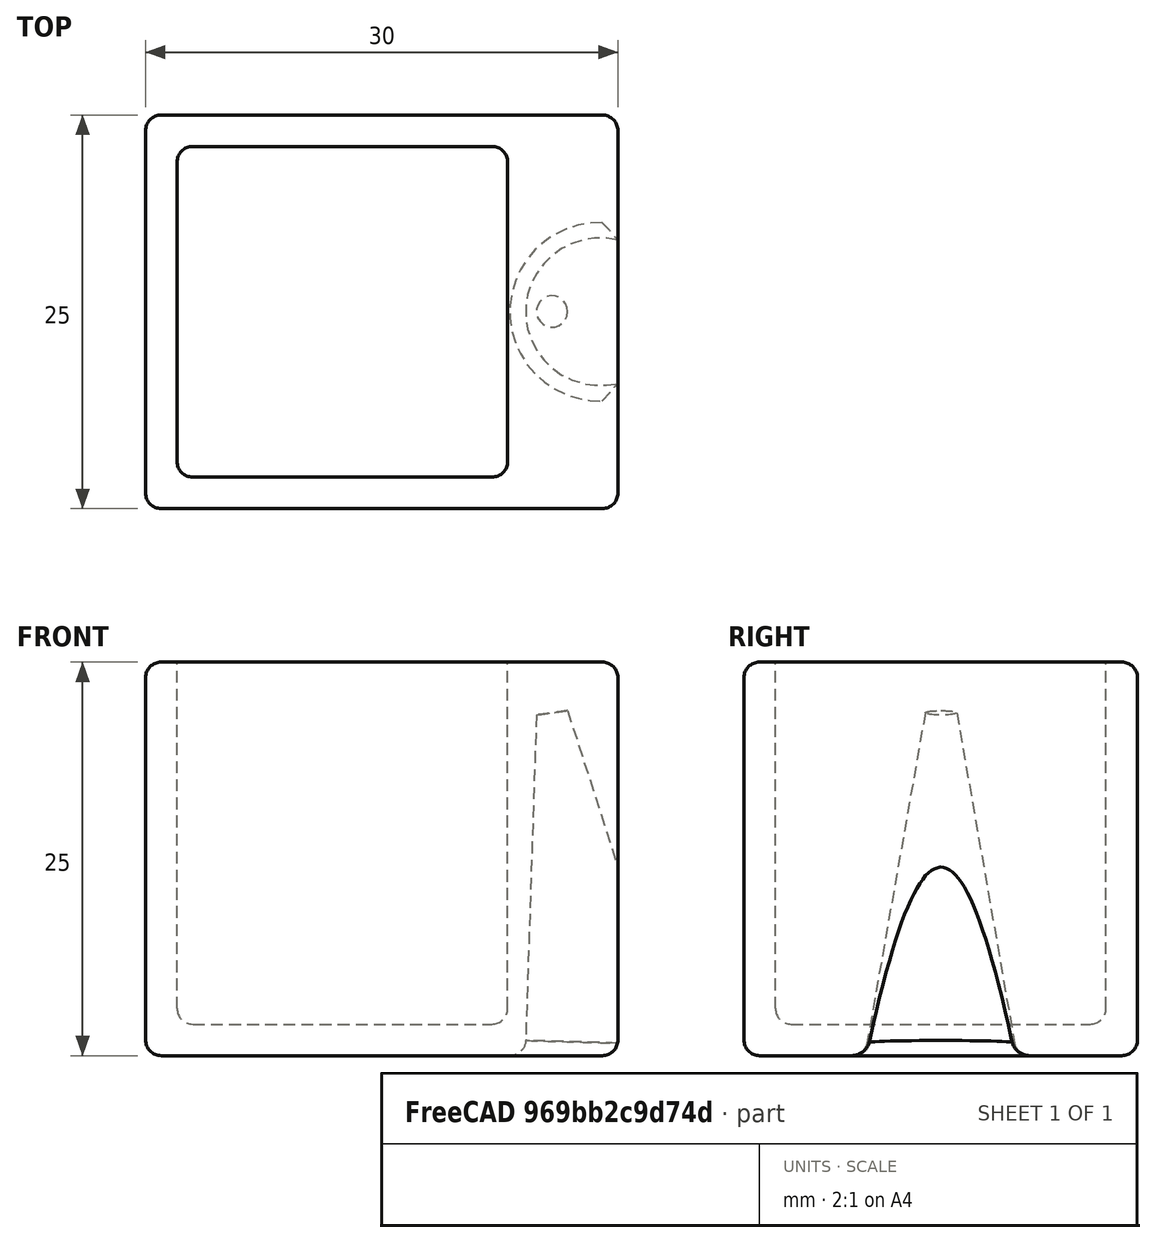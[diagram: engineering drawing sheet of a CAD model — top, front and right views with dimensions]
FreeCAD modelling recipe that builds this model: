
FCSTD DOCUMENT  (FreeCAD 0.18R16117 (Git))
Label: box lift
License: All rights reserved
LicenseURL: http://en.wikipedia.org/wiki/All_rights_reserved
objects: Part::Box×2, Part::Cut×2, Part::Fillet×2, Part::Cone×1
note: 7 computed .brp shape members not serialized (recipe doc carries the construction recipe); baked Part::Feature solids carry a one-line shape summary decoded from their .brp

FEATURE [Part::Box] Box  label="Cube"
  AttacherType = Attacher::AttachEngine3D
  Height = 25
  Length = 30
  Width = 25
FEATURE [Part::Box] Box001  label="Cube001"
  AttacherType = Attacher::AttachEngine3D
  Height = 24
  Length = 21
  Placement = pos=(2,2,2) rot=(0,0,1;0rad)
  Width = 21
FEATURE [Part::Cone] Cone
  Angle = 360
  AttacherType = Attacher::AttachEngine3D
  Height = 23
  Placement = pos=(29,12.5,-1) rot=(0,0.995893,0.090536;-0.139626rad)
  Radius1 = 5
  Radius2 = 1
FEATURE [Part::Cut] Cut
  Base = -> Box
  Tool = -> Cone
FEATURE [Part::Fillet] Fillet
  Base = -> Box001
  Edges = 8 edges r=1: [Edge1,Edge3,Edge4,Edge5,Edge7,Edge8,Edge9,Edge11]
FEATURE [Part::Cut] Cut001
  Base = -> Cut
  Tool = -> Fillet
FEATURE [Part::Fillet] Fillet001
  Base = -> Cut001
  Edges = 14 edges r=1: [Edge1,Edge2,Edge3,Edge4,Edge5,Edge6,Edge7,Edge8,Edge9,Edge18,Edge19,Edge20,Edge21,Edge22]
